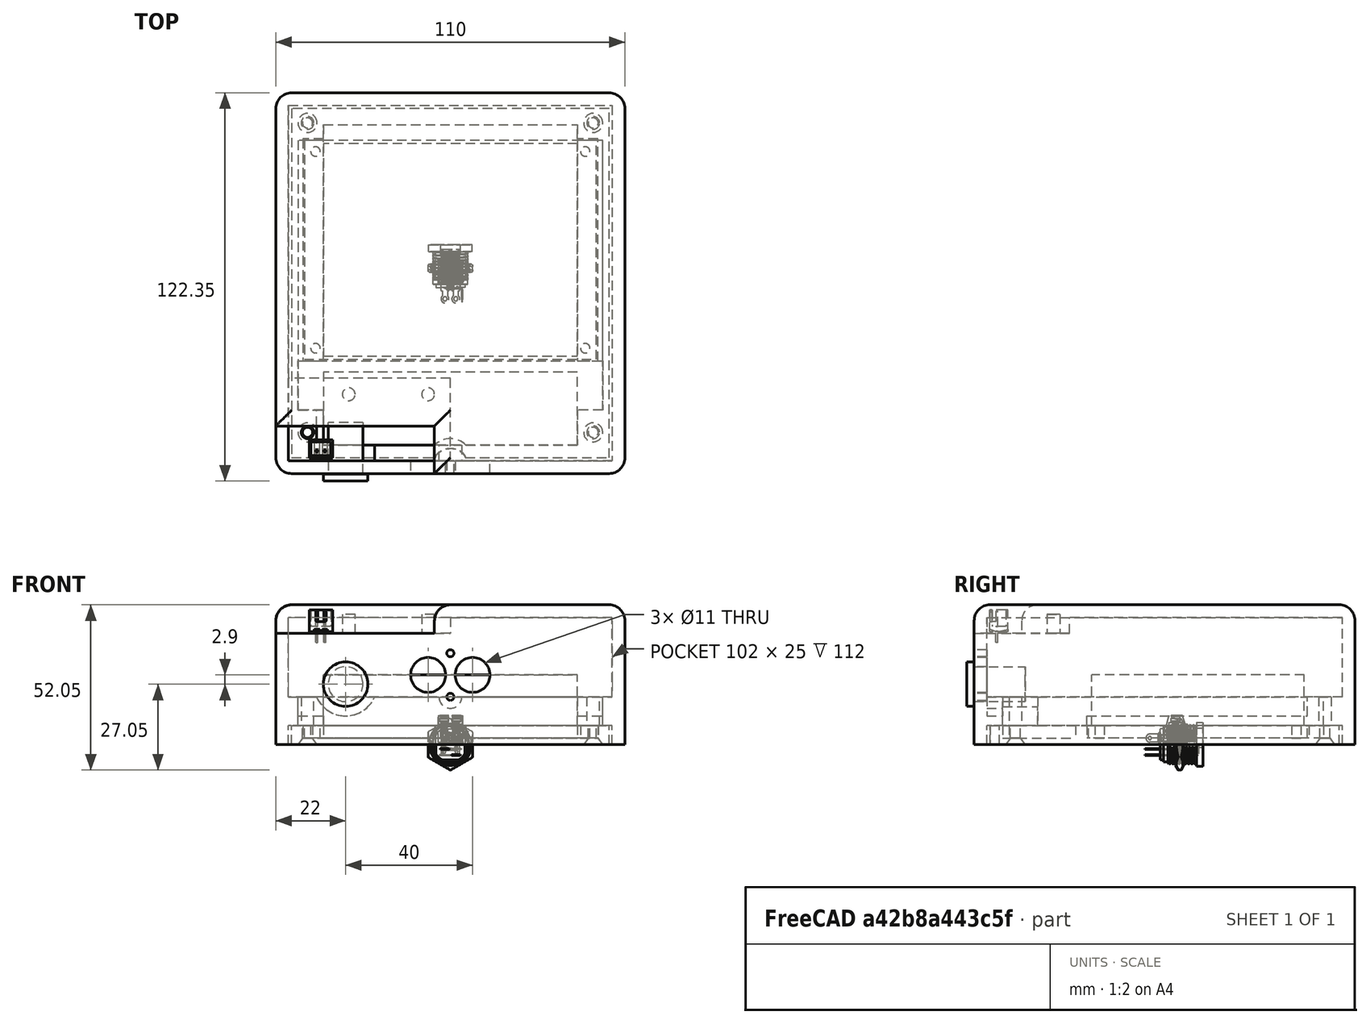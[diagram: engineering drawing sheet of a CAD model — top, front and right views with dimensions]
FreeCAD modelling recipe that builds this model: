
FCSTD DOCUMENT  (FreeCAD 1.0R39109 (Git))
Label: TV External Audio Amplifier
License: All rights reserved
LicenseURL: https://en.wikipedia.org/wiki/All_rights_reserved
objects: Part::Feature×22, Sketcher::SketchObject×14, PartDesign::Pocket×9, PartDesign::Pad×5, PartDesign::Body×4, PartDesign::SubtractiveCone×4, Part::Compound2×3, PartDesign::AdditiveCylinder×3, PartDesign::SubtractiveCylinder×2, Mesh::Feature×1, App::DocumentObjectGroup×1, PartDesign::SubtractiveBox×1, PartDesign::SubtractiveEllipsoid×1, PartDesign::Fillet×1
note: 132 computed .brp shape members not serialized (recipe doc carries the construction recipe); baked Part::Feature solids carry a one-line shape summary decoded from their .brp

FEATURE [Part::Feature] Solid
  shape: bbox 0.8 x 5.207 x 6.922 mm, 20 faces (baked)
FEATURE [Part::Feature] Solid001
  shape: bbox 1.651 x 4.128 x 4.01 mm, 14 faces (baked)
FEATURE [Part::Feature] Solid002
  shape: bbox 2.882 x 2.947 x 4.18 mm, 14 faces (baked)
FEATURE [Part::Feature] Solid003
  shape: bbox 2.882 x 2.947 x 4.18 mm, 14 faces (baked)
FEATURE [Part::Feature] Solid004
  shape: bbox 1.651 x 4.128 x 4.01 mm, 14 faces (baked)
FEATURE [Part::Feature] Solid005
  shape: bbox 7.965 x 7.4 x 8.509 mm, 87 faces (baked)
FEATURE [Part::Feature] Solid006
  shape: bbox 0.8 x 5.207 x 6.922 mm, 20 faces (baked)
FEATURE [Part::Compound2] Compound  label="Amphenol terminal block 2 pin (LEFT)"
  Links = -> [Solid,Solid001,Solid002,Solid003,Solid004,Solid005,Solid006]
  Placement = pos=(-21.1,-56,35) rot=(0,0,1;0rad)
FEATURE [Mesh::Feature] TV_External_Audio_Amplifier_PCB_Mount_2_RCA002  label="2-RCA female audio connector"
  Placement = pos=(-15,-84.4,17.77) rot=(0,-1,0;1.5708rad)
FEATURE [Part::Feature] Solid007  label="JST 2pin PCB mount connector"
  Placement = pos=(-44.5,-65.1,35.5) rot=(-0.57735,0.57735,0.57735;4.18879rad)
  shape: bbox 7.43 x 5.728 x 10.3 mm, 76 faces (baked)
FEATURE [Part::Feature] Solid008
  shape: bbox 14.34 x 12.51 x 14.34 mm, 183 faces (baked)
FEATURE [Part::Feature] Solid009
  shape: bbox 9.1 x 1 x 9.8 mm, 28 faces (baked)
FEATURE [Part::Feature] Solid010
  shape: bbox 3 x 12.2 x 3 mm, 24 faces (baked)
FEATURE [Part::Feature] Solid011
  shape: bbox 5.6 x 4.8 x 3.5 mm, 36 faces (baked)
FEATURE [Part::Feature] Solid012
  shape: bbox 6.8 x 16.05 x 3.518 mm, 44 faces (baked)
FEATURE [Part::Feature] Solid013
  shape: bbox 6.8 x 11 x 0.35 mm, 46 faces (baked)
FEATURE [Part::Feature] Solid014
  shape: bbox 16.11 x 3.852 x 16.11 mm, 38 faces (baked)
FEATURE [Part::Compound2] Compound001  label="Power Connector DS-223B"
  Links = -> [Solid008,Solid009,Solid010,Solid011,Solid012,Solid013,Solid014]
  Placement = pos=(36.5,-70.1,28) rot=(0,0,1;3.14159rad)
FEATURE [Sketcher::SketchObject] Sketch
  ArcFitTolerance = 1e-06
  AttachmentSupport = -> [XY_Plane002]
  FullyConstrained = true
  MakeInternals = false
  MapMode = 5
  sketch-geometry (8):
    g0: LineSegment StartX=-46 StartY=35 StartZ=0 EndX=-46 EndY=-34 EndZ=0
    g1: LineSegment StartX=-46 StartY=-34 StartZ=0 EndX=46 EndY=-34 EndZ=0
    g2: LineSegment StartX=46 StartY=-34 StartZ=0 EndX=46 EndY=35 EndZ=0
    g3: LineSegment StartX=46 StartY=35 StartZ=0 EndX=-46 EndY=35 EndZ=0
    g4: Circle CenterX=-42.5 CenterY=31.5 CenterZ=0 NormalX=0 NormalY=0 NormalZ=1 AngleXU=0 Radius=1.5
    g5: Circle CenterX=42.5 CenterY=31.5 CenterZ=0 NormalX=0 NormalY=0 NormalZ=1 AngleXU=0 Radius=1.5
    g6: Circle CenterX=42.5 CenterY=-30.5 CenterZ=0 NormalX=0 NormalY=0 NormalZ=1 AngleXU=0 Radius=1.5
    g7: Circle CenterX=-42.5 CenterY=-30.5 CenterZ=0 NormalX=0 NormalY=0 NormalZ=1 AngleXU=0 Radius=1.5
  constraints (24):
    c: Coincident(g0,g1)
    c: Coincident(g1,g2)
    c: Coincident(g2,g3)
    c: Coincident(g3,g0)
    c: Vertical(g0)
    c: Vertical(g2)
    c: Horizontal(g1)
    c: Horizontal(g3)
    c: Distance(g0,g2) = 92
    c: Distance(g1,g3) = 69
    c: Distance(g-1,g0) = 46
    c: Distance(g1,g-1) = 34
    c: Diameter(g4) = 3
    c: Diameter(g5) = 3
    c: Diameter(g6) = 3
    c: Diameter(g7) = 3
    c: Distance(g4,g0) = 2
    c: Distance(g4,g3) = 2
    c: Distance(g5,g2) = 2
    c: Distance(g5,g3) = 2
    c: Distance(g7,g1) = 2
    c: Distance(g7,g0) = 2
    c: Distance(g6,g2) = 2
    c: Distance(g6,g1) = 2
FEATURE [PartDesign::Pad] Pad
  Direction = (0,0,1)
  Length = 4
  Length2 = 10
  Profile = -> Sketch
  ReferenceAxis = -> Sketch [N_Axis]
  Refine = true
  Suppressed = false
  Type = 0
FEATURE [Sketcher::SketchObject] Sketch001
  ArcFitTolerance = 1e-06
  AttachmentSupport = -> [XY_Plane]
  FullyConstrained = true
  MakeInternals = false
  MapMode = 5
  sketch-geometry (4):
    g0: LineSegment StartX=-55 StartY=50 StartZ=0 EndX=-55 EndY=-70 EndZ=0
    g1: LineSegment StartX=-55 StartY=-70 StartZ=0 EndX=55 EndY=-70 EndZ=0
    g2: LineSegment StartX=55 StartY=-70 StartZ=0 EndX=55 EndY=50 EndZ=0
    g3: LineSegment StartX=55 StartY=50 StartZ=0 EndX=-55 EndY=50 EndZ=0
  constraints (12):
    c: Coincident(g0,g1)
    c: Coincident(g1,g2)
    c: Coincident(g2,g3)
    c: Coincident(g3,g0)
    c: Vertical(g0)
    c: Vertical(g2)
    c: Horizontal(g1)
    c: Horizontal(g3)
    c: Distance(g0,g2) = 110
    c: Distance(g1,g3) = 120
    c: Distance(g3,g-1) = 50
    c: Distance(g0,g-2) = 55
FEATURE [Sketcher::SketchObject] Sketch003
  ArcFitTolerance = 1e-06
  AttachmentSupport = -> [Pad]
  FullyConstrained = true
  MakeInternals = false
  MapMode = 5
  Placement = pos=(0,0,4) rot=(0,0,1;0rad)
  sketch-geometry (4):
    g0: LineSegment StartX=-40 StartY=34 StartZ=0 EndX=-40 EndY=-33 EndZ=0
    g1: LineSegment StartX=-40 StartY=-33 StartZ=0 EndX=40 EndY=-33 EndZ=0
    g2: LineSegment StartX=40 StartY=-33 StartZ=0 EndX=40 EndY=34 EndZ=0
    g3: LineSegment StartX=40 StartY=34 StartZ=0 EndX=-40 EndY=34 EndZ=0
  constraints (12):
    c: Coincident(g0,g1)
    c: Coincident(g1,g2)
    c: Coincident(g2,g3)
    c: Coincident(g3,g0)
    c: Vertical(g0)
    c: Vertical(g2)
    c: Horizontal(g1)
    c: Horizontal(g3)
    c: Distance(g0,g2) = 80
    c: Distance(g1,g3) = 67
    c: Distance(g-2,g0) = 40
    c: Distance(g-1,g3) = 34
FEATURE [PartDesign::Pad] Pad002
  BaseFeature = -> Pad
  Direction = (0,0,1)
  Length = 16
  Length2 = 10
  Profile = -> Sketch003
  ReferenceAxis = -> Sketch003 [N_Axis]
  Refine = true
  Suppressed = false
  Type = 0
FEATURE [PartDesign::Body] Body002  label="Motherboard"
  AllowCompound = false
  Group = -> [Sketch,Pad,Sketch003,Pad002]
  Origin = -> Origin002
  Placement = pos=(0,0,2) rot=(0,0,1;0rad)
  Tip = -> Pad002
FEATURE [PartDesign::AdditiveCylinder] Cylinder
  Angle = 360
  AttacherType = Attacher::AttachEngine3D
  AttachmentSupport = -> [XZ_Plane003]
  FirstAngle = 0
  Height = 16.2
  MapMode = 5
  Placement = pos=(0,0,0) rot=(1,0,0;1.5708rad)
  Radius = 5.5
  Refine = true
  SecondAngle = 0
  Suppressed = false
  expr: Radius = 11 / 2
FEATURE [PartDesign::AdditiveCylinder] Cylinder001
  Angle = 360
  AttacherType = Attacher::AttachEngine3D
  AttachmentSupport = -> [Cylinder]
  BaseFeature = -> Cylinder
  FirstAngle = 0
  Height = 2.25
  MapMode = 5
  Placement = pos=(0,-16.2,3.6e-15) rot=(1,0,0;1.5708rad)
  Radius = 7
  Refine = true
  SecondAngle = 0
  Suppressed = false
FEATURE [PartDesign::Body] Body003  label="Power Connector (simple)"
  AllowCompound = false
  Group = -> [Cylinder,Cylinder001]
  Origin = -> Origin003
  Placement = pos=(-33,-53.9,19) rot=(0,0,1;0rad)
  Tip = -> Cylinder001
FEATURE [Part::Feature] Solid015
  shape: bbox 0.8 x 5.207 x 6.922 mm, 20 faces (baked)
FEATURE [Part::Feature] Solid016
  shape: bbox 1.651 x 4.128 x 4.01 mm, 14 faces (baked)
FEATURE [Part::Feature] Solid017
  shape: bbox 2.882 x 2.947 x 4.18 mm, 14 faces (baked)
FEATURE [Part::Feature] Solid018
  shape: bbox 2.882 x 2.947 x 4.18 mm, 14 faces (baked)
FEATURE [Part::Feature] Solid019
  shape: bbox 1.651 x 4.128 x 4.01 mm, 14 faces (baked)
FEATURE [Part::Feature] Solid020
  shape: bbox 7.965 x 7.4 x 8.509 mm, 87 faces (baked)
FEATURE [Part::Feature] Solid021
  shape: bbox 0.8 x 5.207 x 6.922 mm, 20 faces (baked)
FEATURE [Part::Compound2] Compound002  label="Amphenol terminal block 2 pin (RIGHT)"
  Links = -> [Solid015,Solid016,Solid017,Solid018,Solid019,Solid020,Solid021]
  Placement = pos=(-13.1,-56,35) rot=(0,0,1;0rad)
FEATURE [App::DocumentObjectGroup] Group  label="Connectors"
  Group = -> [Body003,Compound001,Solid007,TV_External_Audio_Amplifier_PCB_Mount_2_RCA002,Compound,Compound002]
FEATURE [Sketcher::SketchObject] Sketch007
  ArcFitTolerance = 1e-06
  AttachmentSupport = -> [XY_Plane001]
  FullyConstrained = true
  MakeInternals = false
  MapMode = 5
  sketch-geometry (4):
    g0: LineSegment StartX=-50 StartY=45 StartZ=0 EndX=-50 EndY=-65 EndZ=0
    g1: LineSegment StartX=-50 StartY=-65 StartZ=0 EndX=50 EndY=-65 EndZ=0
    g2: LineSegment StartX=50 StartY=-65 StartZ=0 EndX=50 EndY=45 EndZ=0
    g3: LineSegment StartX=50 StartY=45 StartZ=0 EndX=-50 EndY=45 EndZ=0
  constraints (12):
    c: Coincident(g0,g1)
    c: Coincident(g1,g2)
    c: Coincident(g2,g3)
    c: Coincident(g3,g0)
    c: Vertical(g0)
    c: Vertical(g2)
    c: Horizontal(g1)
    c: Horizontal(g3)
    c: Distance(g0,g2) = 100
    c: Distance(g1,g3) = 110
    c: Distance(g3,g-1) = 45
    c: Distance(g0,g-2) = 50
FEATURE [PartDesign::Pad] Pad004
  Direction = (0,0,1)
  Length = 6
  Length2 = 10
  Profile = -> Sketch007
  ReferenceAxis = -> Sketch007 [N_Axis]
  Refine = true
  Suppressed = false
  Type = 0
FEATURE [Sketcher::SketchObject] Sketch008
  ArcFitTolerance = 1e-06
  AttachmentSupport = -> [Pad004]
  FullyConstrained = true
  MakeInternals = false
  MapMode = 5
  Placement = pos=(0,0,6) rot=(0,0,1;0rad)
  sketch-geometry (12):
    g0: LineSegment StartX=-46.5 StartY=35.5 StartZ=0 EndX=-46.5 EndY=-34.5 EndZ=0
    g1: LineSegment StartX=-46.5 StartY=-34.5 StartZ=0 EndX=46.5 EndY=-34.5 EndZ=0
    g2: LineSegment StartX=46.5 StartY=-34.5 StartZ=0 EndX=46.5 EndY=35.5 EndZ=0
    g3: LineSegment StartX=46.5 StartY=35.5 StartZ=0 EndX=-46.5 EndY=35.5 EndZ=0
    g4: LineSegment StartX=-40 StartY=-38 StartZ=0 EndX=-40 EndY=-61 EndZ=0
    g5: LineSegment StartX=-40 StartY=-61 StartZ=0 EndX=40 EndY=-61 EndZ=0
    g6: LineSegment StartX=40 StartY=-61 StartZ=0 EndX=40 EndY=-38 EndZ=0
    g7: LineSegment StartX=40 StartY=-38 StartZ=0 EndX=-40 EndY=-38 EndZ=0
    g8: LineSegment StartX=-40 StartY=40 StartZ=0 EndX=-40 EndY=35 EndZ=0
    g9: LineSegment StartX=-40 StartY=35 StartZ=0 EndX=40 EndY=35 EndZ=0
    g10: LineSegment StartX=40 StartY=35 StartZ=0 EndX=40 EndY=40 EndZ=0
    g11: LineSegment StartX=40 StartY=40 StartZ=0 EndX=-40 EndY=40 EndZ=0
  constraints (36):
    c: Coincident(g0,g1)
    c: Coincident(g1,g2)
    c: Coincident(g2,g3)
    c: Coincident(g3,g0)
    c: Vertical(g0)
    c: Vertical(g2)
    c: Horizontal(g1)
    c: Horizontal(g3)
    c: Distance(g0,g2) = 93
    c: Distance(g1,g3) = 70
    c: Distance(g0,g-2) = 46.5
    c: DistanceY(g-1,g2) = 35.5
    c: Coincident(g4,g5)
    c: Coincident(g5,g6)
    c: Coincident(g6,g7)
    c: Coincident(g7,g4)
    c: Vertical(g4)
    c: Vertical(g6)
    c: Horizontal(g5)
    c: Horizontal(g7)
    c: Distance(g4,g6) = 80
    c: Distance(g5,g7) = 23
    c: Coincident(g8,g9)
    c: Coincident(g9,g10)
    c: Coincident(g10,g11)
    c: Coincident(g11,g8)
    c: Vertical(g8)
    c: Vertical(g10)
    c: Horizontal(g9)
    c: Horizontal(g11)
    c: Equal(g7,g11)
    c: Distance(g4,g-2) = 40
    c: Distance(g6,g-1) = 38
    c: Distance(g8,g-2) = 40
    c: Distance(g9,g-1) = 35
    c: Distance(g8,g8) = 5
FEATURE [PartDesign::Pocket] Pocket  label="PCB Holder spacing"
  BaseFeature = -> Pad004
  Direction = (0,0,-1)
  Length = 4
  Length2 = 5
  Profile = -> Sketch008
  ReferenceAxis = -> Sketch008 [N_Axis]
  Refine = true
  Suppressed = false
  Type = 0
FEATURE [Sketcher::SketchObject] Sketch009
  ArcFitTolerance = 1e-06
  AttachmentSupport = -> [Pocket]
  FullyConstrained = true
  MakeInternals = false
  MapMode = 5
  Placement = pos=(0,0,6) rot=(0,0,1;0rad)
  sketch-geometry (4):
    g0: Circle CenterX=-45 CenterY=40.5 CenterZ=0 NormalX=0 NormalY=0 NormalZ=1 AngleXU=0 Radius=1.6
    g1: Circle CenterX=45 CenterY=40.5 CenterZ=0 NormalX=0 NormalY=0 NormalZ=1 AngleXU=0 Radius=1.6
    g2: Circle CenterX=-45 CenterY=-57 CenterZ=0 NormalX=0 NormalY=0 NormalZ=1 AngleXU=0 Radius=1.6
    g3: Circle CenterX=45 CenterY=-57 CenterZ=0 NormalX=0 NormalY=0 NormalZ=1 AngleXU=0 Radius=1.6
  constraints (12):
    c: Diameter(g0) = 3.2
    c: Diameter(g1) = 3.2
    c: Diameter(g2) = 3.2
    c: Diameter(g3) = 3.2
    c: Distance(g2,g-1) = 57
    c: Distance(g3,g-1) = 57
    c: Distance(g0,g-1) = 40.5
    c: Distance(g0,g-2) = 45
    c: Distance(g1,g-2) = 45
    c: Distance(g2,g-2) = 45
    c: Distance(g3,g-2) = 45
    c: Distance(g1,g-1) = 40.5
FEATURE [PartDesign::Pocket] Pocket001  label="Box Holes"
  BaseFeature = -> Pocket
  Direction = (0,0,-1)
  Length = 5
  Length2 = 5
  Profile = -> Sketch009
  ReferenceAxis = -> Sketch009 [N_Axis]
  Refine = true
  Suppressed = false
  Type = 1
FEATURE [PartDesign::SubtractiveCone] Cone
  Angle = 360
  AttacherType = Attacher::AttachEngine3D
  AttachmentOffset = pos=(-45,-57,0) rot=(0,0,1;0rad)
  AttachmentSupport = -> [XY_Plane001]
  BaseFeature = -> Pocket001
  Height = 2
  MapMode = 5
  Placement = pos=(-45,-57,0) rot=(0,0,1;0rad)
  Radius1 = 3
  Radius2 = 1.6
  Refine = true
  Suppressed = false
FEATURE [PartDesign::SubtractiveCone] Cone001
  Angle = 360
  AttacherType = Attacher::AttachEngine3D
  AttachmentOffset = pos=(45,-57,0) rot=(0,0,1;0rad)
  AttachmentSupport = -> [XY_Plane001]
  BaseFeature = -> Cone
  Height = 2
  MapMode = 5
  Placement = pos=(45,-57,0) rot=(0,0,1;0rad)
  Radius1 = 3
  Radius2 = 1.6
  Refine = true
  Suppressed = false
FEATURE [PartDesign::SubtractiveCone] Cone002
  Angle = 360
  AttacherType = Attacher::AttachEngine3D
  AttachmentOffset = pos=(45,40.5,0) rot=(0,0,1;0rad)
  AttachmentSupport = -> [XY_Plane001]
  BaseFeature = -> Cone001
  Height = 2
  MapMode = 5
  Placement = pos=(45,40.5,0) rot=(0,0,1;0rad)
  Radius1 = 3
  Radius2 = 1.6
  Refine = true
  Suppressed = false
FEATURE [PartDesign::SubtractiveCone] Cone003
  Angle = 360
  AttacherType = Attacher::AttachEngine3D
  AttachmentOffset = pos=(-45,40.5,0) rot=(0,0,1;0rad)
  AttachmentSupport = -> [XY_Plane001]
  BaseFeature = -> Cone002
  Height = 2
  MapMode = 5
  Placement = pos=(-45,40.5,0) rot=(0,0,1;0rad)
  Radius1 = 3
  Radius2 = 1.6
  Refine = true
  Suppressed = false
FEATURE [PartDesign::Pad] Pad005  label="base box"
  Direction = (0,0,1)
  Length = 44
  Length2 = 10
  Profile = -> Sketch001
  ReferenceAxis = -> Sketch001 [N_Axis]
  Refine = true
  Suppressed = false
  Type = 0
FEATURE [Sketcher::SketchObject] Sketch002
  ArcFitTolerance = 1e-06
  AttachmentSupport = -> [Pad005]
  FullyConstrained = true
  MakeInternals = false
  MapMode = 5
  Placement = pos=(0,0,0) rot=(1,0,0;3.14159rad)
  sketch-geometry (4):
    g0: LineSegment StartX=-51 StartY=66 StartZ=0 EndX=-51 EndY=-46 EndZ=0
    g1: LineSegment StartX=-51 StartY=-46 StartZ=0 EndX=51 EndY=-46 EndZ=0
    g2: LineSegment StartX=51 StartY=-46 StartZ=0 EndX=51 EndY=66 EndZ=0
    g3: LineSegment StartX=51 StartY=66 StartZ=0 EndX=-51 EndY=66 EndZ=0
  constraints (12):
    c: Coincident(g0,g1)
    c: Coincident(g1,g2)
    c: Coincident(g2,g3)
    c: Coincident(g3,g0)
    c: Vertical(g0)
    c: Vertical(g2)
    c: Horizontal(g1)
    c: Horizontal(g3)
    c: Distance(g0,g2) = 102
    c: Distance(g1,g3) = 112
    c: Distance(g-2,g0) = 51
    c: Distance(g-1,g1) = 46
FEATURE [PartDesign::Pocket] Pocket002  label="hole box bottom"
  BaseFeature = -> Pad005
  Direction = (0,0,1)
  Length = 6
  Length2 = 5
  Profile = -> Sketch002
  ReferenceAxis = -> Sketch002 [N_Axis]
  Refine = true
  Suppressed = false
  Type = 0
FEATURE [Sketcher::SketchObject] Sketch010
  ArcFitTolerance = 1e-06
  AttachmentSupport = -> [Pocket002]
  FullyConstrained = true
  MakeInternals = false
  MapMode = 5
  Placement = pos=(0,0,6) rot=(1,0,0;3.14159rad)
  sketch-geometry (12):
    g0: Circle CenterX=-45 CenterY=57 CenterZ=0 NormalX=0 NormalY=0 NormalZ=1 AngleXU=0 Radius=2
    g1: Circle CenterX=45 CenterY=57 CenterZ=0 NormalX=0 NormalY=0 NormalZ=1 AngleXU=0 Radius=2
    g2: Circle CenterX=45 CenterY=-40.5 CenterZ=0 NormalX=0 NormalY=0 NormalZ=1 AngleXU=0 Radius=2
    g3: Circle CenterX=-45 CenterY=-40.5 CenterZ=0 NormalX=0 NormalY=0 NormalZ=1 AngleXU=0 Radius=2
    g4: LineSegment StartX=-40 StartY=61 StartZ=0 EndX=-40 EndY=-40 EndZ=0
    g5: LineSegment StartX=-40 StartY=-40 StartZ=0 EndX=40 EndY=-40 EndZ=0
    g6: LineSegment StartX=40 StartY=-40 StartZ=0 EndX=40 EndY=61 EndZ=0
    g7: LineSegment StartX=40 StartY=61 StartZ=0 EndX=-40 EndY=61 EndZ=0
    g8: LineSegment StartX=-48 StartY=34.5 StartZ=0 EndX=48 EndY=34.5 EndZ=0
    g9: LineSegment StartX=48 StartY=34.5 StartZ=0 EndX=48 EndY=50 EndZ=0
    g10: LineSegment StartX=48 StartY=50 StartZ=0 EndX=-48 EndY=50 EndZ=0
    g11: LineSegment StartX=-48 StartY=50 StartZ=0 EndX=-48 EndY=34.5 EndZ=0
  constraints (36):
    c: Diameter(g0) = 4
    c: Diameter(g1) = 4
    c: Diameter(g2) = 4
    c: Diameter(g3) = 4
    c: Distance(g3,g-2) = 45
    c: Distance(g3,g-1) = 40.5
    c: Distance(g2,g-1) = 40.5
    c: Distance(g2,g-2) = 45
    c: Distance(g0,g-1) = 57
    c: Distance(g0,g-2) = 45
    c: Distance(g1,g-2) = 45
    c: Distance(g1,g-1) = 57
    c: Coincident(g4,g5)
    c: Coincident(g5,g6)
    c: Coincident(g6,g7)
    c: Coincident(g7,g4)
    c: Vertical(g4)
    c: Vertical(g6)
    c: Horizontal(g5)
    c: Horizontal(g7)
    c: Distance(g4,g6) = 80
    c: Distance(g5,g7) = 101
    c: Distance(g4,g-2) = 40
    c: DistanceY(g5,g-1) = 40
    c: Coincident(g8,g9)
    c: Coincident(g9,g10)
    c: Coincident(g10,g11)
    c: Coincident(g11,g8)
    c: Horizontal(g8)
    c: Horizontal(g10)
    c: Vertical(g9)
    c: Vertical(g11)
    c: Distance(g9,g11) = 96
    c: Distance(g8,g10) = 15.5
    c: Distance(g8,g-2) = 48
    c: Distance(g8,g-1) = 34.5
FEATURE [PartDesign::Pocket] Pocket003  label="hole box bottom PCB handle"
  BaseFeature = -> Pocket002
  Direction = (0,0,1)
  Length = 10
  Length2 = 5
  Profile = -> Sketch010
  ReferenceAxis = -> Sketch010 [N_Axis]
  Refine = true
  Suppressed = false
  Type = 0
FEATURE [Sketcher::SketchObject] Sketch011
  ArcFitTolerance = 1e-06
  AttachmentOffset = pos=(0,0,9) rot=(0,0,1;0rad)
  AttachmentSupport = -> [XY_Plane]
  FullyConstrained = true
  MakeInternals = false
  MapMode = 5
  Placement = pos=(0,0,9) rot=(0,0,1;0rad)
  sketch-geometry (4):
    g0: LineSegment StartX=-48 StartY=35 StartZ=0 EndX=-48 EndY=-50 EndZ=0
    g1: LineSegment StartX=-48 StartY=-50 StartZ=0 EndX=48 EndY=-50 EndZ=0
    g2: LineSegment StartX=48 StartY=-50 StartZ=0 EndX=48 EndY=35 EndZ=0
    g3: LineSegment StartX=48 StartY=35 StartZ=0 EndX=-48 EndY=35 EndZ=0
  constraints (12):
    c: Coincident(g0,g1)
    c: Coincident(g1,g2)
    c: Coincident(g2,g3)
    c: Coincident(g3,g0)
    c: Vertical(g0)
    c: Vertical(g2)
    c: Horizontal(g1)
    c: Horizontal(g3)
    c: Distance(g0,g-2) = 48
    c: DistanceX(g3,g3) = 96
    c: DistanceY(g0,g0) = 85
    c: DistanceY(g-1,g0) = 35
FEATURE [Sketcher::SketchObject] Sketch012
  ArcFitTolerance = 1e-06
  AttachmentOffset = pos=(0,0,15) rot=(0,0,1;0rad)
  AttachmentSupport = -> [XY_Plane]
  FullyConstrained = true
  MakeInternals = false
  MapMode = 5
  Placement = pos=(0,0,15) rot=(0,0,1;0rad)
  sketch-geometry (4):
    g0: LineSegment StartX=-51 StartY=46 StartZ=0 EndX=-51 EndY=-66 EndZ=0
    g1: LineSegment StartX=-51 StartY=-66 StartZ=0 EndX=51 EndY=-66 EndZ=0
    g2: LineSegment StartX=51 StartY=-66 StartZ=0 EndX=51 EndY=46 EndZ=0
    g3: LineSegment StartX=51 StartY=46 StartZ=0 EndX=-51 EndY=46 EndZ=0
  constraints (12):
    c: Coincident(g0,g1)
    c: Coincident(g1,g2)
    c: Coincident(g2,g3)
    c: Coincident(g3,g0)
    c: Vertical(g0)
    c: Vertical(g2)
    c: Horizontal(g1)
    c: Horizontal(g3)
    c: Distance(g0,g-2) = 51
    c: DistanceX(g3,g3) = 102
    c: DistanceY(g0,g0) = 112
    c: DistanceY(g-1,g0) = 46
FEATURE [PartDesign::Pocket] Pocket004  label="pcb frame holder"
  BaseFeature = -> Pocket003
  Direction = (0,0,-1)
  Length = 7
  Length2 = 5
  Profile = -> Sketch011
  ReferenceAxis = -> Sketch011 [N_Axis]
  Refine = true
  Reversed = true
  Suppressed = false
  Type = 0
FEATURE [PartDesign::Pocket] Pocket005  label="Inner Hole"
  BaseFeature = -> Pocket004
  Direction = (0,0,-1)
  Length = 25
  Length2 = 5
  Profile = -> Sketch012
  ReferenceAxis = -> Sketch012 [N_Axis]
  Refine = true
  Reversed = true
  Suppressed = false
  Type = 0
FEATURE [PartDesign::AdditiveCylinder] Cylinder002
  Angle = 360
  AttacherType = Attacher::AttachEngine3D
  AttachmentOffset = pos=(0,-66,0) rot=(0,0,1;0rad)
  AttachmentSupport = -> [XY_Plane001]
  BaseFeature = -> Cone003
  FirstAngle = 0
  Height = 6
  MapMode = 5
  Placement = pos=(0,-66,0) rot=(0,0,1;0rad)
  Radius = 7
  Refine = true
  SecondAngle = 0
  Suppressed = false
FEATURE [PartDesign::SubtractiveBox] Box
  AttacherType = Attacher::AttachEngine3D
  AttachmentOffset = pos=(-8,-75,0) rot=(0,0,1;0rad)
  AttachmentSupport = -> [XY_Plane001]
  BaseFeature = -> Cylinder002
  Height = 6
  Length = 16
  MapMode = 5
  Placement = pos=(-8,-75,0) rot=(0,0,1;0rad)
  Refine = true
  Suppressed = false
  Width = 10
FEATURE [PartDesign::SubtractiveEllipsoid] Ellipsoid
  Angle1 = -90
  Angle2 = 90
  Angle3 = 360
  AttacherType = Attacher::AttachEngine3D
  AttachmentOffset = pos=(0,-66,3) rot=(0,0,1;0rad)
  AttachmentSupport = -> [XY_Plane001]
  BaseFeature = -> Box
  MapMode = 5
  Placement = pos=(0,-66,3) rot=(0,0,1;0rad)
  Radius1 = 14
  Radius2 = 5
  Radius3 = 4
  Refine = true
  Suppressed = false
FEATURE [PartDesign::Body] Body001  label="Box Bottom"
  AllowCompound = false
  Group = -> [Sketch007,Pad004,Sketch008,Pocket,Sketch009,Pocket001,Cone,Cone001,Cone002,Cone003,Cylinder002,Box,Ellipsoid]
  Origin = -> Origin001
  Tip = -> Ellipsoid
FEATURE [Sketcher::SketchObject] Sketch013
  ArcFitTolerance = 1e-06
  AttachmentSupport = -> [Pocket005]
  FullyConstrained = true
  MakeInternals = false
  MapMode = 5
  Placement = pos=(0,0,44) rot=(0,0,1;0rad)
  sketch-geometry (4):
    g0: LineSegment StartX=-55 StartY=-55 StartZ=0 EndX=-55 EndY=-70 EndZ=0
    g1: LineSegment StartX=-55 StartY=-70 StartZ=0 EndX=-5 EndY=-70 EndZ=0
    g2: LineSegment StartX=-5 StartY=-70 StartZ=0 EndX=-5 EndY=-55 EndZ=0
    g3: LineSegment StartX=-5 StartY=-55 StartZ=0 EndX=-55 EndY=-55 EndZ=0
  constraints (12):
    c: Coincident(g0,g1)
    c: Coincident(g1,g2)
    c: Coincident(g2,g3)
    c: Coincident(g3,g0)
    c: Vertical(g0)
    c: Vertical(g2)
    c: Horizontal(g1)
    c: Horizontal(g3)
    c: Distance(g0,g2) = 50
    c: Distance(g1,g3) = 15
    c: Distance(g0,g-1) = 55
    c: Distance(g2,g-2) = 5
FEATURE [Sketcher::SketchObject] Sketch014
  ArcFitTolerance = 1e-06
  AttachmentSupport = -> [Pocket005]
  FullyConstrained = true
  MakeInternals = false
  MapMode = 5
  Placement = pos=(0,0,44) rot=(0,0,1;0rad)
  sketch-geometry (4):
    g0: LineSegment StartX=-55 StartY=-40 StartZ=0 EndX=-55 EndY=-70 EndZ=0
    g1: LineSegment StartX=-55 StartY=-70 StartZ=0 EndX=0 EndY=-70 EndZ=0
    g2: LineSegment StartX=0 StartY=-70 StartZ=0 EndX=0 EndY=-40 EndZ=0
    g3: LineSegment StartX=0 StartY=-40 StartZ=0 EndX=-55 EndY=-40 EndZ=0
  constraints (12):
    c: Coincident(g0,g1)
    c: Coincident(g1,g2)
    c: Coincident(g2,g3)
    c: Coincident(g3,g0)
    c: Vertical(g0)
    c: Vertical(g2)
    c: Horizontal(g1)
    c: Horizontal(g3)
    c: Distance(g0,g2) = 55
    c: Distance(g1,g3) = 30
    c: Distance(g0,g-1) = 40
    c: PointOnObject(g1,g-2)
FEATURE [PartDesign::Pad] Pad006
  BaseFeature = -> Pocket005
  Direction = (0,0,1)
  Length = 9
  Length2 = 10
  Profile = -> Sketch014
  ReferenceAxis = -> Sketch014 [N_Axis]
  Refine = true
  Reversed = true
  Suppressed = false
  Type = 0
FEATURE [PartDesign::Pocket] Pocket006
  BaseFeature = -> Pad006
  Direction = (0,0,-1)
  Length = 9
  Length2 = 5
  Profile = -> Sketch013
  ReferenceAxis = -> Sketch013 [N_Axis]
  Refine = true
  Suppressed = false
  Type = 0
FEATURE [PartDesign::Fillet] Fillet
  Base = -> Pocket006 [Face10,Edge9,Edge13,Edge19,Edge14]
  BaseFeature = -> Pocket006
  Radius = 5
  Refine = true
  SupportTransform = false
  Suppressed = false
  UseAllEdges = false
FEATURE [Sketcher::SketchObject] Sketch015
  ArcFitTolerance = 1e-06
  AttachmentSupport = -> [Fillet]
  FullyConstrained = true
  MakeInternals = false
  MapMode = 5
  Placement = pos=(0,0,35) rot=(1,0,0;3.14159rad)
  sketch-geometry (2):
    g0: Circle CenterX=-7 CenterY=45 CenterZ=0 NormalX=0 NormalY=0 NormalZ=1 AngleXU=0 Radius=2
    g1: Circle CenterX=-32 CenterY=45 CenterZ=0 NormalX=0 NormalY=0 NormalZ=1 AngleXU=0 Radius=2
  constraints (6):
    c: Diameter(g0) = 4
    c: Diameter(g1) = 4
    c: Distance(g1,g-2) = 32
    c: DistanceX(g0,g-1) = 7
    c: DistanceY(g-1,g1) = 45
    c: DistanceY(g-1,g0) = 45
FEATURE [PartDesign::Pocket] Pocket007
  BaseFeature = -> Fillet
  Direction = (0,0,1)
  Length = 6
  Length2 = 5
  Profile = -> Sketch015
  ReferenceAxis = -> Sketch015 [N_Axis]
  Refine = true
  Suppressed = false
  Type = 0
FEATURE [Sketcher::SketchObject] Sketch016
  ArcFitTolerance = 1e-06
  AttachmentSupport = -> [Pocket007]
  FullyConstrained = true
  MakeInternals = false
  MapMode = 5
  Placement = pos=(0,-70,0) rot=(1,0,0;1.5708rad)
  sketch-geometry (5):
    g0: Circle CenterX=-7 CenterY=21.9 CenterZ=0 NormalX=0 NormalY=0 NormalZ=1 AngleXU=0 Radius=5.5
    g1: Circle CenterX=7 CenterY=21.9 CenterZ=0 NormalX=0 NormalY=0 NormalZ=1 AngleXU=0 Radius=5.5
    g2: Circle CenterX=0 CenterY=28.75 CenterZ=0 NormalX=0 NormalY=0 NormalZ=1 AngleXU=0 Radius=1.125
    g3: Circle CenterX=0 CenterY=15 CenterZ=0 NormalX=0 NormalY=0 NormalZ=1 AngleXU=0 Radius=1.125
    g4: Circle CenterX=-33 CenterY=19 CenterZ=0 NormalX=0 NormalY=0 NormalZ=1 AngleXU=0 Radius=5.5
  constraints (15):
    c: Diameter(g0) = 11
    c: Diameter(g1) = 11
    c: DistanceY(g-1,g0) = 21.9
    c: DistanceY(g-1,g1) = 21.9
    c: Distance(g0,g-2) = 7
    c: Distance(g1,g-2) = 7
    c: Diameter(g2) = 2.25
    c: PointOnObject(g2,g-2)
    c: Diameter(g3) = 2.25
    c: PointOnObject(g3,g-2)
    c: DistanceY(g-1,g3) = 15
    c: DistanceY(g-1,g2) = 28.75
    c: Diameter(g4) = 11
    c: DistanceY(g-1,g4) = 19
    c: DistanceX(g4,g-1) = 33
FEATURE [PartDesign::SubtractiveCylinder] Cylinder003
  Angle = 360
  AttacherType = Attacher::AttachEngine3D
  AttachmentOffset = pos=(0,15,61) rot=(0,0,1;0rad)
  AttachmentSupport = -> [XZ_Plane]
  BaseFeature = -> Pocket007
  FirstAngle = 0
  Height = 5
  MapMode = 5
  Placement = pos=(0,-61,15) rot=(1,0,0;1.5708rad)
  Radius = 3.6
  Refine = true
  SecondAngle = 0
  Suppressed = false
FEATURE [PartDesign::SubtractiveCylinder] Cylinder004
  Angle = 360
  AttacherType = Attacher::AttachEngine3D
  AttachmentOffset = pos=(-33,19,50) rot=(0,0,1;0rad)
  AttachmentSupport = -> [XZ_Plane]
  BaseFeature = -> Cylinder003
  FirstAngle = 0
  Height = 16
  MapMode = 5
  Placement = pos=(-33,-50,19) rot=(1,0,0;1.5708rad)
  Radius = 10
  Refine = true
  SecondAngle = 0
  Suppressed = false
FEATURE [PartDesign::Pocket] Pocket008
  BaseFeature = -> Cylinder004
  Direction = (0,1,-2e-16)
  Length = 4
  Length2 = 5
  Placement = pos=(-33,-50,19) rot=(1,0,0;1.5708rad)
  Profile = -> Sketch016
  ReferenceAxis = -> Sketch016 [N_Axis]
  Refine = true
  Suppressed = false
  Type = 0
FEATURE [PartDesign::Body] Body  label="Box Top"
  AllowCompound = false
  Group = -> [Sketch001,Sketch002,Pad005,Pocket002,Sketch010,Pocket003,Sketch011,Sketch012,Pocket004,Pocket005,Sketch013,Sketch014,Pad006,Pocket006,Fillet,Sketch015,Pocket007,Sketch016,Cylinder003,Cylinder004,Pocket008]
  Origin = -> Origin
  Tip = -> Pocket008
